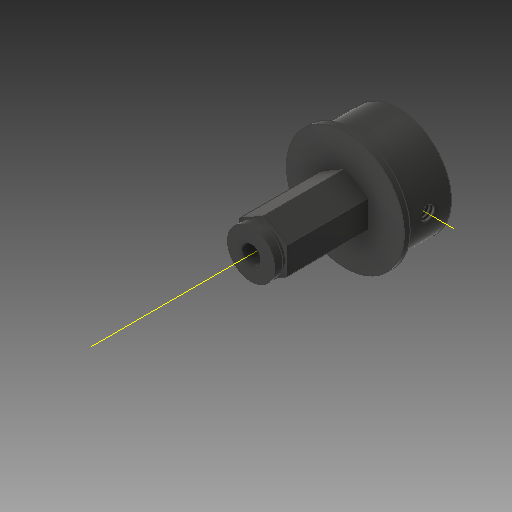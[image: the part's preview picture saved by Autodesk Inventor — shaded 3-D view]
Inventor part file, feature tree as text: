
AUTODESK INVENTOR PART (.ipt)
format: ipt  version: 2019.4 (Build 234330000, 330)  size: 184,320 bytes
history: native  units: in
note: dims shown in document units (in); Inventor stores cm internally (conversion verified against a paired STEP export)
features: sketch x8, extrude x5, projected_geometry x5, hole x2, plane x1, mirror x1, revolve x1, other x1
ambient origin geometry x8: Origin, YZ Plane, XZ Plane, XY Plane, X Axis, Y Axis, Z Axis, Center Point
bodies: Solid1 (feature_tree)
feature tree (24):
  extrude  "Extrusion1"  Depth=1.0in TaperAngle=0.0deg
  extrude  "Extrusion2"  Depth=0.0625in TaperAngle=0.0deg
  extrude  "Extrusion3"  Depth=0.5in TaperAngle=0.0deg
  hole  "Hole1"  [1 undecoded]
  plane  "Work Plane1"
  hole  "Hole2"  [1 undecoded]
  mirror  "Mirror1"
  extrude  "Extrusion4"  Depth=0.375in TaperAngle=0.0deg
  revolve  "Revolution1"  [1 undecoded]
  extrude  "Extrusion5"  [1 undecoded]
  other  "Work Axis1"
  sketch  "Sketch1"  dims[d0=0.5in d1=1.0in d2=0.0in]
  sketch  "Sketch2"  dims[d3=1.25in d4=0.0625in d5=0.0in]
  sketch  "Sketch3"  dims[d6=1.125in d7=0.5in d8=0.0in]
  sketch  "Sketch4"  dims[d9=0.196in d10=0.5in d11=0.375in d12=0.25in d13=0.5635in d14=1.0in d15=0.8108in]
  sketch  "Sketch5"  dims[d16=0.145in d17=0.375in d18=0.375in d19=0.25in d20=0.5635in d21=0.375in d22=0.0in d23=0.125in d24=0.0in]
  projected_geometry  "Projected Loop1"
  sketch  "Sketch6"  dims[d25=0.0125in d26=0.0375in]
  projected_geometry  "Projected Loop2"
  sketch  "Sketch7"  dims[d27=90.0deg d28=0.375in d29=0.0in]
  sketch  "Sketch8"
  projected_geometry  "Projected Loop3"
  projected_geometry  "Projected Loop4"
  projected_geometry  "Project Cut Edges1"
note: 4 required parameter values undecoded (feature->parameter linkage not recoverable at this tier; creation-order binding heuristic only, values carry confidence <= 0.55)
